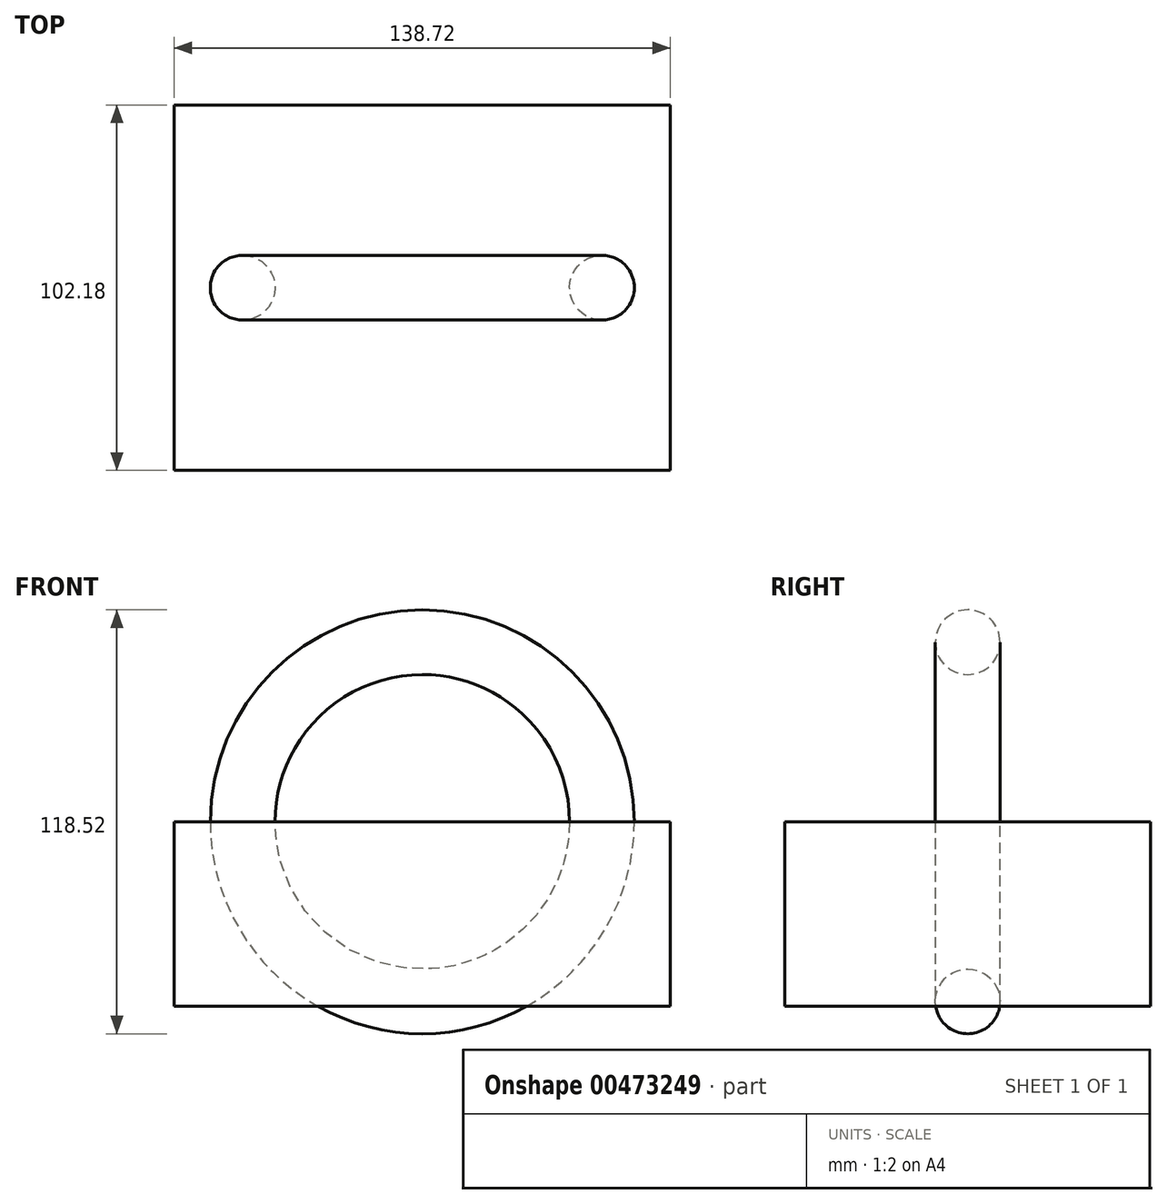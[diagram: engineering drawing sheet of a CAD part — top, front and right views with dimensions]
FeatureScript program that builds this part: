
annotation { "Feature Type Name" : "Feature", "Feature Type Description" : "" }
export const myFeature = defineFeature(function(context is Context, id is Id, definition is map)
    precondition{}
    {
        {
            var Q0;
            Q0=qCreatedBy(makeId("Top.planeOp"),FACE);
            var sketch = newSketch(context, id + "F0", { "sketchPlane" : qUnion([Q0])});
            skLineSegment(sketch, "E0.bottom", {"start": v(69.36, -51.1) * mm, "end": v(-69.36, -51.1) * mm});
            skLineSegment(sketch, "E0.top", {"start": v(69.36, 51.1) * mm, "end": v(-69.36, 51.1) * mm});
            skLineSegment(sketch, "E0.left", {"start": v(69.36, -51.1) * mm, "end": v(69.36, 51.1) * mm});
            skLineSegment(sketch, "E0.right", {"start": v(-69.36, -51.1) * mm, "end": v(-69.36, 51.1) * mm});
            skPoint(sketch, "E0.middle", {"position": v(0, 0) * mm});
            skLineSegment(sketch, "E1", {"start": v(0, 51.1) * mm, "end": v(0, -51.1) * mm});
            skSolve(sketch);
        }
        {
            var Q0;
            Q0=qCreatedBy(makeId("Top.planeOp"),FACE);
            var sketch = newSketch(context, id + "F1", { "sketchPlane" : qUnion([Q0])});
            skCircle(sketch, "E2", {"center": v(50.21, 0) * mm, "radius": 9.05 * mm});
            skSolve(sketch);
        }
        {
            var Q0;
            {var subQ0=sQuery(id+"F0.wireOp",EDGE,"E0.left");Q0=makeQuery(id+"F0.imprint","IMPRINT",FACE,{"disambiguationData":[TD([[makeQuery(id+"F0.imprint","IMPRINT",EDGE,{"derivedFrom":subQ0}),1.0]])]});}
            var Q1;
            {var subQ0=sQuery(id+"F0.wireOp",EDGE,"E0.right");Q1=makeQuery(id+"F0.imprint","IMPRINT",FACE,{"disambiguationData":[TD([[makeQuery(id+"F0.imprint","IMPRINT",EDGE,{"derivedFrom":subQ0}),-1.0]])]});}
            extrude(context, id + "F2", {"entities" : qUnion([Q0, Q1]), "oppositeDirection" : true, "depth" : 51.56 * mm});
        }
        {
            var Q0;
            Q0=makeQuery(id+"F1.imprint","IMPRINT",FACE,{"disambiguationData":[TD([[makeQuery(id+"F1.imprint","IMPRINT",EDGE,{"derivedFrom":sQuery(id+"F1.wireOp",EDGE,"E2")}),1.0]])]});
            var Q1;
            Q1=sQuery(id+"F0.wireOp",EDGE,"E1");
            revolve(context, id + "F3", {"entities" : qUnion([Q0]), "axis" : qUnion([Q1]), "revolveType" : RevolveType.FULL});
        }
    });
